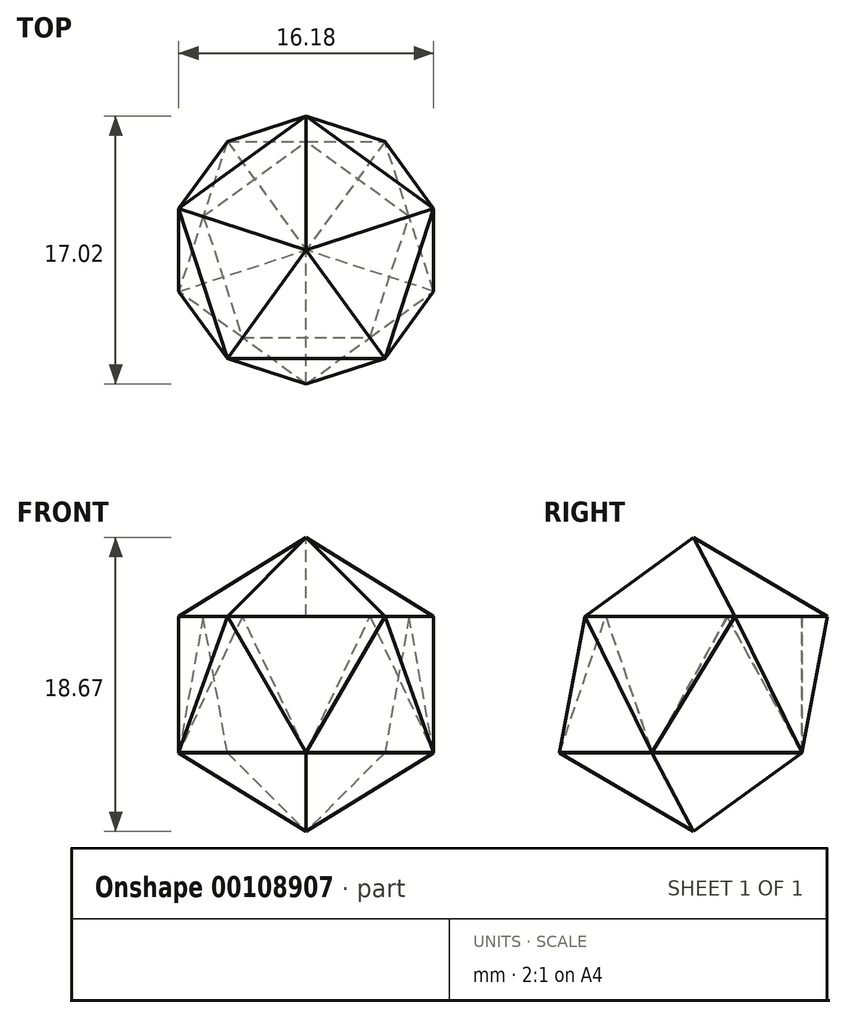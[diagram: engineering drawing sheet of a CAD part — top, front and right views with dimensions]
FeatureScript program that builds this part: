
annotation { "Feature Type Name" : "Feature", "Feature Type Description" : "" }
export const myFeature = defineFeature(function(context is Context, id is Id, definition is map)
    precondition{}
    {
        {
            var Q0;
            Q0=qCreatedBy(makeId("Top.planeOp"),FACE);
            var sketch = newSketch(context, id + "F0", { "sketchPlane" : qUnion([Q0])});
            skCircle(sketch, "E0.cCircle", {"center": v(0, 0) * mm, "radius": 6.88 * mm, "construction": true});
            skLineSegment(sketch, "E0.0", {"start": v(5, -6.88) * mm, "end": v(-5, -6.88) * mm});
            skLineSegment(sketch, "E0.1", {"start": v(-5, -6.88) * mm, "end": v(-8.1, 2.63) * mm});
            skLineSegment(sketch, "E0.2", {"start": v(-8.1, 2.63) * mm, "end": v(0, 8.5) * mm});
            skLineSegment(sketch, "E0.3", {"start": v(0, 8.5) * mm, "end": v(8.1, 2.63) * mm});
            skLineSegment(sketch, "E0.4", {"start": v(8.1, 2.63) * mm, "end": v(5, -6.88) * mm});
            skPoint(sketch, "E0.0.midPoint", {"position": v(0, -6.88) * mm});
            skLineSegment(sketch, "E1", {"start": v(-5, -6.88) * mm, "end": v(0, 0) * mm});
            skSolve(sketch);
        }
        {
            var Q0;
            Q0=qCreatedBy(makeId("Top.planeOp"),FACE);
            cPlane(context, id + "F1", {"entities" : qUnion([Q0]), "cplaneType" : CPlaneType.OFFSET, "offset" : 5 * mm, "width" : 150 * mm, "height" : 150 * mm});
        }
        {
            var Q0;
            Q0=qCreatedBy(id+"F1.planeOp",FACE);
            var sketch = newSketch(context, id + "F2", { "sketchPlane" : qUnion([Q0])});
            skPoint(sketch, "E2", {"position": v(0, 0) * mm});
            skSolve(sketch);
        }
        {
            var Q0;
            Q0=makeQuery(id+"F0.imprint","IMPRINT",FACE,{"disambiguationData":[TD([[makeQuery(id+"F0.imprint","IMPRINT",EDGE,{"derivedFrom":sQuery(id+"F0.wireOp",EDGE,"E0.0")}),-1.0]])]});
            var Q1;
            Q1=sQuery(id+"F2.wireOp",VERTEX,"E2");
            loft(context, id + "F3", {"sheetProfilesArray" : [{ "sheetProfileEntities" : qUnion([Q0]) }, { "sheetProfileEntities" : qUnion([Q1]) }]});
        }
        {
            var Q0;
            Q0=makeQuery(id+"F0.imprint","IMPRINT",FACE,{"disambiguationData":[TD([[makeQuery(id+"F0.imprint","IMPRINT",EDGE,{"derivedFrom":sQuery(id+"F0.wireOp",EDGE,"E0.0")}),-1.0]])]});
            cPlane(context, id + "F4", {"entities" : qUnion([Q0]), "cplaneType" : CPlaneType.OFFSET, "offset" : 8.66 * mm, "oppositeDirection" : true, "width" : 150 * mm, "height" : 150 * mm});
        }
        {
            var Q0;
            Q0=qCreatedBy(id+"F4.planeOp",FACE);
            var sketch = newSketch(context, id + "F5", { "sketchPlane" : qUnion([Q0])});
            skCircle(sketch, "E3.cCircle", {"center": v(0, 0) * mm, "radius": 6.88 * mm, "construction": true});
            skLineSegment(sketch, "E3.0", {"start": v(8.1, -2.63) * mm, "end": v(0, -8.5) * mm});
            skLineSegment(sketch, "E3.1", {"start": v(0, -8.5) * mm, "end": v(-8.09, -2.63) * mm});
            skLineSegment(sketch, "E3.2", {"start": v(-8.09, -2.63) * mm, "end": v(-5, 6.88) * mm});
            skLineSegment(sketch, "E3.3", {"start": v(-5, 6.88) * mm, "end": v(5, 6.88) * mm});
            skLineSegment(sketch, "E3.4", {"start": v(5, 6.88) * mm, "end": v(8.1, -2.63) * mm});
            skPoint(sketch, "E3.0.midPoint", {"position": v(4.05, -5.57) * mm});
            skSolve(sketch);
        }
        {
            var Q0;
            Q0=makeQuery(id+"F5.imprint","IMPRINT",FACE,{"disambiguationData":[TD([[makeQuery(id+"F5.imprint","IMPRINT",EDGE,{"derivedFrom":sQuery(id+"F5.wireOp",EDGE,"E3.0")}),-1.0]])]});
            extrude(context, id + "F6", {"entities" : qUnion([Q0]), "oppositeDirection" : true, "depth" : 0.01 * mm});
        }
        {
            var Q0;
            Q0=makeQuery(id+"F6.opExtrude","SWEPT_FACE",FACE,{"disambiguationData":[OSD([sQuery(id+"F5.wireOp",EDGE,"E3.2")])]});
            var sketch = newSketch(context, id + "F7", { "sketchPlane" : qUnion([Q0])});
            skPoint(sketch, "E4", {"position": v(-0.02, -0.03) * mm});
            skLineSegment(sketch, "E5", {"start": v(-5, -8.66) * mm, "end": v(-0.02, -0.03) * mm});
            skLineSegment(sketch, "E6", {"start": v(-0.02, -0.03) * mm, "end": v(5, -8.66) * mm});
            skSolve(sketch);
        }
        {
            var Q0;
            Q0=makeQuery(id+"F7.imprint","IMPRINT",FACE,{"disambiguationData":[TD([[makeQuery(id+"F7.imprint","IMPRINT",EDGE,{"derivedFrom":sQuery(id+"F7.wireOp",EDGE,"E5")}),-1.0]])]});
            var Q1;
            Q1=makeQuery(id+"F3.opLoft","MID_CAP_VERTEX",VERTEX,{"disambiguationData":[OSD([sQuery(id+"F0.wireOp",EDGE,"E0.1"),sQuery(id+"F0.wireOp",EDGE,"E0.2")])],"capPos":0.0});
            loft(context, id + "F8", {"sheetProfilesArray" : [{ "sheetProfileEntities" : qUnion([Q0]) }, { "sheetProfileEntities" : qUnion([Q1]) }]});
        }
        {
            var Q0;
            Q0=makeQuery(id+"F6.opExtrude","SWEPT_FACE",FACE,{"disambiguationData":[OSD([sQuery(id+"F5.wireOp",EDGE,"E3.1")])]});
            var sketch = newSketch(context, id + "F9", { "sketchPlane" : qUnion([Q0])});
            skLineSegment(sketch, "E7", {"start": v(0, 0) * mm, "end": v(-5, -8.66) * mm});
            skLineSegment(sketch, "E8", {"start": v(-5, -8.66) * mm, "end": v(5, -8.66) * mm});
            skLineSegment(sketch, "E9", {"start": v(5, -8.66) * mm, "end": v(0, 0) * mm});
            skSolve(sketch);
        }
        {
            var Q1;
            Q1=makeQuery(id+"F9.imprint","IMPRINT",FACE,{"disambiguationData":[TD([[makeQuery(id+"F9.imprint","IMPRINT",EDGE,{"derivedFrom":sQuery(id+"F9.wireOp",EDGE,"E7")}),1.0]])]});
            var Q2;
            Q2=makeQuery(id+"F3.opLoft","MID_CAP_VERTEX",VERTEX,{"disambiguationData":[OSD([sQuery(id+"F0.wireOp",EDGE,"E0.0"),sQuery(id+"F0.wireOp",EDGE,"E0.1")])],"capPos":0.0});
            loft(context, id + "F10", {"operationType" : NewBodyOperationType.ADD, "sheetProfilesArray" : [{ "sheetProfileEntities" : qUnion([Q1]) }, { "sheetProfileEntities" : qUnion([Q2]) }]});
        }
        {
            var Q0;
            Q0=makeQuery(id+"F8.opLoft","SWEPT_FACE",FACE,{"disambiguationData":[OSD([sQuery(id+"F5.wireOp",EDGE,"E3.1"),sQuery(id+"F5.wireOp",EDGE,"E3.2"),sQuery(id+"F7.wireOp",EDGE,"E5"),sQuery(id+"F7.wireOp",EDGE,"E6")])]});
            var Q1;
            Q1=makeQuery(id+"F10.opLoft","SWEPT_FACE",FACE,{"disambiguationData":[OSD([sQuery(id+"F5.wireOp",EDGE,"E3.1"),sQuery(id+"F5.wireOp",EDGE,"E3.2"),sQuery(id+"F9.wireOp",EDGE,"E7"),sQuery(id+"F9.wireOp",EDGE,"E8"),sQuery(id+"F9.wireOp",EDGE,"E9")])]});
            loft(context, id + "F11", {"sheetProfilesArray" : [{ "sheetProfileEntities" : qUnion([Q0]) }, { "sheetProfileEntities" : qUnion([Q1]) }]});
        }
        {
            var Q0;
            Q0=makeQuery(id+"F6.opExtrude","SWEPT_FACE",FACE,{"disambiguationData":[OSD([sQuery(id+"F5.wireOp",EDGE,"E3.3")])]});
            var sketch = newSketch(context, id + "F12", { "sketchPlane" : qUnion([Q0])});
            skLineSegment(sketch, "E10", {"start": v(0, 0) * mm, "end": v(-5, -8.66) * mm});
            skLineSegment(sketch, "E11", {"start": v(-5, -8.66) * mm, "end": v(5, -8.66) * mm});
            skLineSegment(sketch, "E12", {"start": v(5, -8.66) * mm, "end": v(0, 0) * mm});
            skSolve(sketch);
        }
        {
            var Q1;
            Q1=makeQuery(id+"F12.imprint","IMPRINT",FACE,{"disambiguationData":[TD([[makeQuery(id+"F12.imprint","IMPRINT",EDGE,{"derivedFrom":sQuery(id+"F12.wireOp",EDGE,"E10")}),1.0]])]});
            var Q2;
            Q2=makeQuery(id+"F3.opLoft","MID_CAP_VERTEX",VERTEX,{"disambiguationData":[OSD([sQuery(id+"F0.wireOp",EDGE,"E0.2"),sQuery(id+"F0.wireOp",EDGE,"E0.3")])],"capPos":0.0});
            loft(context, id + "F13", {"operationType" : NewBodyOperationType.ADD, "sheetProfilesArray" : [{ "sheetProfileEntities" : qUnion([Q1]) }, { "sheetProfileEntities" : qUnion([Q2]) }]});
        }
        {
            var Q0;
            Q0=makeQuery(id+"F8.opLoft","SWEPT_FACE",FACE,{"disambiguationData":[OSD([sQuery(id+"F5.wireOp",EDGE,"E3.2"),sQuery(id+"F5.wireOp",EDGE,"E3.3"),sQuery(id+"F7.wireOp",EDGE,"E5"),sQuery(id+"F7.wireOp",EDGE,"E6")])]});
            var Q1;
            Q1=makeQuery(id+"F13.opLoft","SWEPT_FACE",FACE,{"disambiguationData":[OSD([sQuery(id+"F5.wireOp",EDGE,"E3.2"),sQuery(id+"F5.wireOp",EDGE,"E3.3"),sQuery(id+"F12.wireOp",EDGE,"E10"),sQuery(id+"F12.wireOp",EDGE,"E11"),sQuery(id+"F12.wireOp",EDGE,"E12")])]});
            loft(context, id + "F14", {"sheetProfilesArray" : [{ "sheetProfileEntities" : qUnion([Q0]) }, { "sheetProfileEntities" : qUnion([Q1]) }]});
        }
        {
            var Q0;
            Q0=makeQuery(id+"F6.opExtrude","SWEPT_FACE",FACE,{"disambiguationData":[OSD([sQuery(id+"F5.wireOp",EDGE,"E3.0")])]});
            var sketch = newSketch(context, id + "F15", { "sketchPlane" : qUnion([Q0])});
            skLineSegment(sketch, "E13", {"start": v(-5, -8.66) * mm, "end": v(0, -0.02) * mm});
            skLineSegment(sketch, "E14", {"start": v(0, -0.02) * mm, "end": v(5, -8.66) * mm});
            skLineSegment(sketch, "E15", {"start": v(5, -8.66) * mm, "end": v(-5, -8.66) * mm});
            skSolve(sketch);
        }
        {
            var Q0;
            Q0=makeQuery(id+"F3.opLoft","MID_CAP_VERTEX",VERTEX,{"disambiguationData":[OSD([sQuery(id+"F0.wireOp",EDGE,"E0.0"),sQuery(id+"F0.wireOp",EDGE,"E0.4")])],"capPos":0.0});
            var Q1;
            Q1=makeQuery(id+"F15.imprint","IMPRINT",FACE,{"disambiguationData":[TD([[makeQuery(id+"F15.imprint","IMPRINT",EDGE,{"derivedFrom":sQuery(id+"F15.wireOp",EDGE,"E13")}),-1.0]])]});
            loft(context, id + "F16", {"sheetProfilesArray" : [{ "sheetProfileEntities" : qUnion([Q0]) }, { "sheetProfileEntities" : qUnion([Q1]) }]});
        }
        {
            var Q0;
            Q0=makeQuery(id+"F10.opLoft","SWEPT_FACE",FACE,{"disambiguationData":[OSD([sQuery(id+"F5.wireOp",EDGE,"E3.0"),sQuery(id+"F5.wireOp",EDGE,"E3.1"),sQuery(id+"F9.wireOp",EDGE,"E7"),sQuery(id+"F9.wireOp",EDGE,"E8"),sQuery(id+"F9.wireOp",EDGE,"E9")])]});
            var Q1;
            Q1=makeQuery(id+"F16.opLoft","SWEPT_FACE",FACE,{"disambiguationData":[OSD([sQuery(id+"F5.wireOp",EDGE,"E3.0"),sQuery(id+"F5.wireOp",EDGE,"E3.1"),sQuery(id+"F15.wireOp",EDGE,"E13"),sQuery(id+"F15.wireOp",EDGE,"E14"),sQuery(id+"F15.wireOp",EDGE,"E15")])]});
            loft(context, id + "F17", {"sheetProfilesArray" : [{ "sheetProfileEntities" : qUnion([Q0]) }, { "sheetProfileEntities" : qUnion([Q1]) }]});
        }
        {
            var Q0;
            Q0=makeQuery(id+"F6.opExtrude","SWEPT_FACE",FACE,{"disambiguationData":[OSD([sQuery(id+"F5.wireOp",EDGE,"E3.4")])]});
            var sketch = newSketch(context, id + "F18", { "sketchPlane" : qUnion([Q0])});
            skLineSegment(sketch, "E16", {"start": v(-5, -8.66) * mm, "end": v(0, -0.02) * mm});
            skLineSegment(sketch, "E17", {"start": v(0, -0.02) * mm, "end": v(5, -8.66) * mm});
            skLineSegment(sketch, "E18", {"start": v(5, -8.66) * mm, "end": v(-5, -8.66) * mm});
            skSolve(sketch);
        }
        {
            var Q0;
            Q0=makeQuery(id+"F18.imprint","IMPRINT",FACE,{"disambiguationData":[TD([[makeQuery(id+"F18.imprint","IMPRINT",EDGE,{"derivedFrom":sQuery(id+"F18.wireOp",EDGE,"E16")}),-1.0]])]});
            var Q1;
            Q1=makeQuery(id+"F3.opLoft","MID_CAP_VERTEX",VERTEX,{"disambiguationData":[OSD([sQuery(id+"F0.wireOp",EDGE,"E0.3"),sQuery(id+"F0.wireOp",EDGE,"E0.4")])],"capPos":0.0});
            loft(context, id + "F19", {"sheetProfilesArray" : [{ "sheetProfileEntities" : qUnion([Q0]) }, { "sheetProfileEntities" : qUnion([Q1]) }]});
        }
        {
            var Q0;
            Q0=makeQuery(id+"F16.opLoft","SWEPT_FACE",FACE,{"disambiguationData":[OSD([sQuery(id+"F5.wireOp",EDGE,"E3.0"),sQuery(id+"F5.wireOp",EDGE,"E3.4"),sQuery(id+"F15.wireOp",EDGE,"E13"),sQuery(id+"F15.wireOp",EDGE,"E14"),sQuery(id+"F15.wireOp",EDGE,"E15")])]});
            var Q1;
            Q1=makeQuery(id+"F19.opLoft","SWEPT_FACE",FACE,{"disambiguationData":[OSD([sQuery(id+"F5.wireOp",EDGE,"E3.0"),sQuery(id+"F5.wireOp",EDGE,"E3.4"),sQuery(id+"F18.wireOp",EDGE,"E16"),sQuery(id+"F18.wireOp",EDGE,"E17"),sQuery(id+"F18.wireOp",EDGE,"E18")])]});
            loft(context, id + "F20", {"sheetProfilesArray" : [{ "sheetProfileEntities" : qUnion([Q0]) }, { "sheetProfileEntities" : qUnion([Q1]) }]});
        }
        {
            var Q0;
            Q0=makeQuery(id+"F19.opLoft","SWEPT_FACE",FACE,{"disambiguationData":[OSD([sQuery(id+"F5.wireOp",EDGE,"E3.3"),sQuery(id+"F5.wireOp",EDGE,"E3.4"),sQuery(id+"F18.wireOp",EDGE,"E16"),sQuery(id+"F18.wireOp",EDGE,"E17"),sQuery(id+"F18.wireOp",EDGE,"E18")])]});
            var sketch = newSketch(context, id + "F21", { "sketchPlane" : qUnion([Q0])});
            skLineSegment(sketch, "E19", {"start": v(-5.18, -10.98) * mm, "end": v(-8.4, -1.37) * mm});
            skLineSegment(sketch, "E20", {"start": v(-8.4, -1.37) * mm, "end": v(-6.79, -1.13) * mm});
            skLineSegment(sketch, "E21", {"start": v(-6.79, -1.13) * mm, "end": v(-5.18, -10.98) * mm});
            skSolve(sketch);
        }
        {
            var Q0;
            Q0=makeQuery(id+"F21.imprint","IMPRINT",FACE,{"disambiguationData":[TD([[makeQuery(id+"F21.imprint","IMPRINT",EDGE,{"derivedFrom":sQuery(id+"F21.wireOp",EDGE,"E19")}),-1.0]])]});
            var Q1;
            Q1=makeQuery(id+"F13.opLoft","SWEPT_FACE",FACE,{"disambiguationData":[OSD([sQuery(id+"F5.wireOp",EDGE,"E3.3"),sQuery(id+"F5.wireOp",EDGE,"E3.4"),sQuery(id+"F12.wireOp",EDGE,"E10"),sQuery(id+"F12.wireOp",EDGE,"E11"),sQuery(id+"F12.wireOp",EDGE,"E12")])]});
            loft(context, id + "F22", {"sheetProfilesArray" : [{ "sheetProfileEntities" : qUnion([Q0]) }, { "sheetProfileEntities" : qUnion([Q1]) }]});
        }
        {
            var Q0;
            Q0=makeQuery(id+"F6.opExtrude","CAP_FACE",FACE,{"disambiguationData":[OSD([sQuery(id+"F5.wireOp",EDGE,"E3.0"),sQuery(id+"F5.wireOp",EDGE,"E3.1"),sQuery(id+"F5.wireOp",EDGE,"E3.2"),sQuery(id+"F5.wireOp",EDGE,"E3.3"),sQuery(id+"F5.wireOp",EDGE,"E3.4")])],"isStart":false});
            cPlane(context, id + "F23", {"entities" : qUnion([Q0]), "cplaneType" : CPlaneType.OFFSET, "offset" : 5 * mm, "width" : 150 * mm, "height" : 150 * mm});
        }
        {
            var Q0;
            Q0=qCreatedBy(id+"F23.planeOp",FACE);
            var sketch = newSketch(context, id + "F24", { "sketchPlane" : qUnion([Q0])});
            skPoint(sketch, "E22", {"position": v(0, 0) * mm});
            skSolve(sketch);
        }
        {
            var Q1;
            Q1=makeQuery(id+"F6.opExtrude","CAP_FACE",FACE,{"disambiguationData":[OSD([sQuery(id+"F5.wireOp",EDGE,"E3.0"),sQuery(id+"F5.wireOp",EDGE,"E3.1"),sQuery(id+"F5.wireOp",EDGE,"E3.2"),sQuery(id+"F5.wireOp",EDGE,"E3.3"),sQuery(id+"F5.wireOp",EDGE,"E3.4")])],"isStart":false});
            var Q2;
            Q2=sQuery(id+"F24.wireOp",VERTEX,"E22");
            loft(context, id + "F25", {"operationType" : NewBodyOperationType.ADD, "sheetProfilesArray" : [{ "sheetProfileEntities" : qUnion([Q1]) }, { "sheetProfileEntities" : qUnion([Q2]) }]});
        }
        {
            var Q0;
            Q0=qCreatedBy(id+"F23.planeOp",FACE);
            cPlane(context, id + "F26", {"entities" : qUnion([Q0]), "cplaneType" : CPlaneType.OFFSET, "offset" : 5 * mm, "oppositeDirection" : true, "width" : 150 * mm, "height" : 150 * mm});
        }
    });
